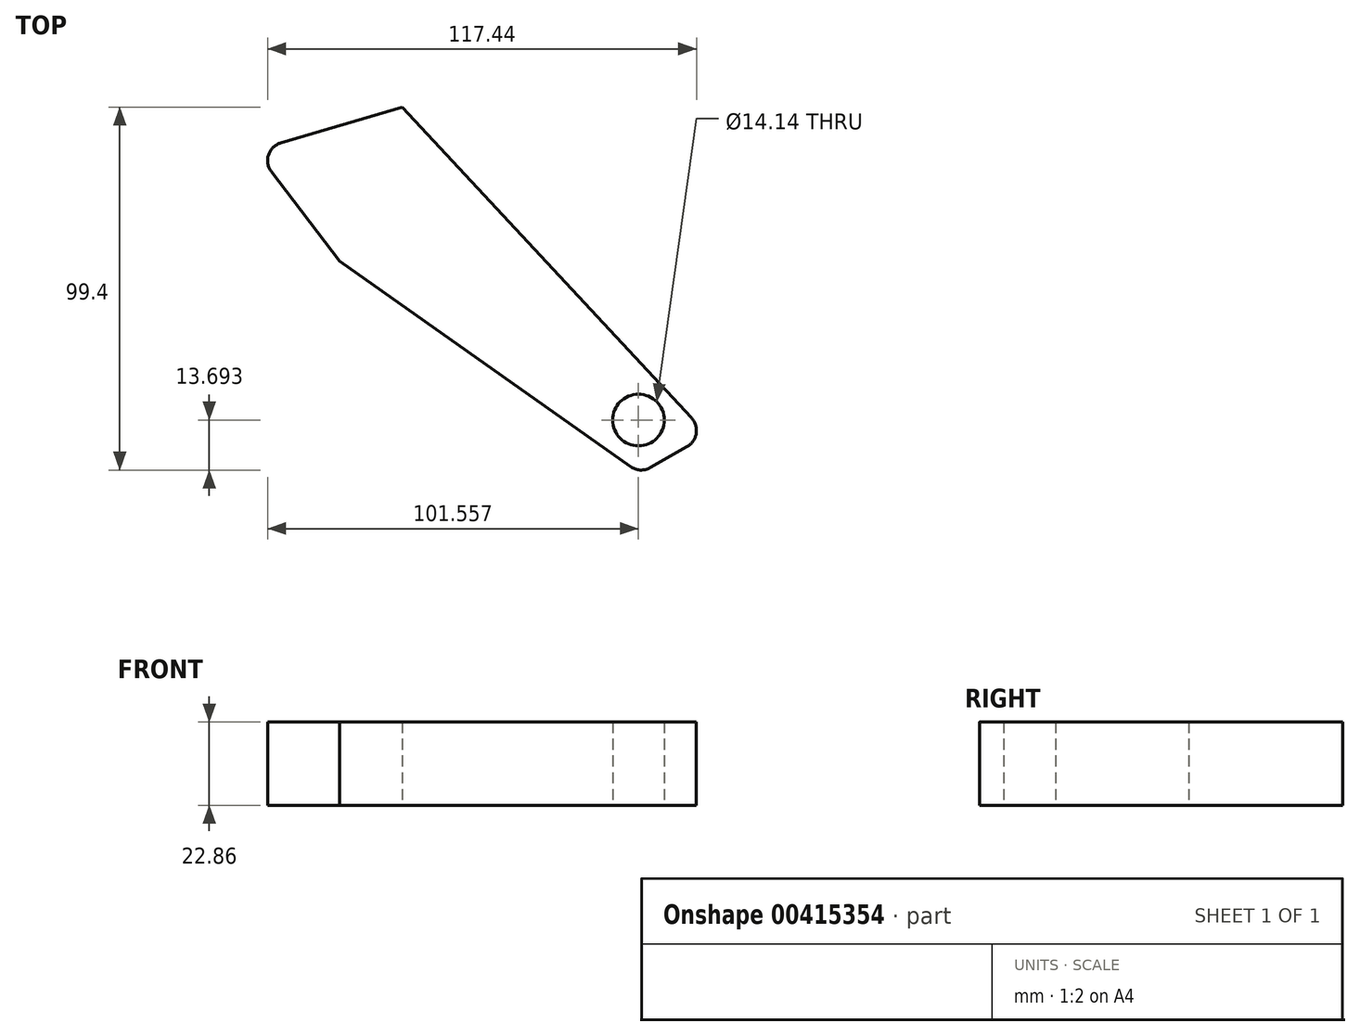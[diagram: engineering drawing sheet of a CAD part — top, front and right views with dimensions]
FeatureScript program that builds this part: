
annotation { "Feature Type Name" : "Feature", "Feature Type Description" : "" }
export const myFeature = defineFeature(function(context is Context, id is Id, definition is map)
    precondition{}
    {
        {
            var Q0;
            Q0=qCreatedBy(makeId("Top.planeOp"),FACE);
            var sketch = newSketch(context, id + "F0", { "sketchPlane" : qUnion([Q0])});
            skLineSegment(sketch, "E0", {"start": v(55.04, -31.63) * mm, "end": v(-28.5, 58.2) * mm});
            skLineSegment(sketch, "E1", {"start": v(-68.84, 46.34) * mm, "end": v(-28.5, 58.2) * mm});
            skLineSegment(sketch, "E2", {"start": v(-68.84, 46.34) * mm, "end": v(-45.74, 16.05) * mm});
            skLineSegment(sketch, "E3", {"start": v(-45.74, 16.05) * mm, "end": v(36.6, -42.14) * mm});
            skLineSegment(sketch, "E4", {"start": v(36.6, -42.14) * mm, "end": v(55.04, -31.63) * mm});
            skSolve(sketch);
        }
        {
            var Q0;
            Q0 = qSketchRegion(id + "F0", true);
            extrude(context, id + "F1", {"entities" : qUnion([Q0]), "depth" : 0.03 * yard});
        }
        {
            var Q0;
            Q0=makeQuery(id+"F1.opExtrude","SWEPT_EDGE",EDGE,{"disambiguationData":[OSD([sQuery(id+"F0.wireOp",EDGE,"E1"),sQuery(id+"F0.wireOp",EDGE,"E2")])]});
            fillet(context, id + "F2", {"entities" : qUnion([Q0]), "radius" : 5.08 * mm, "tangentPropagation" : true, "allowEdgeOverflow" : false});
        }
        {
            var Q0;
            Q0=makeQuery(id+"F1.opExtrude","SWEPT_EDGE",EDGE,{"disambiguationData":[OSD([sQuery(id+"F0.wireOp",EDGE,"E3"),sQuery(id+"F0.wireOp",EDGE,"E4")])]});
            fillet(context, id + "F3", {"entities" : qUnion([Q0]), "radius" : 5.08 * mm, "tangentPropagation" : true, "allowEdgeOverflow" : false});
        }
        {
            var Q0;
            Q0=makeQuery(id+"F1.opExtrude","SWEPT_EDGE",EDGE,{"disambiguationData":[OSD([sQuery(id+"F0.wireOp",EDGE,"E0"),sQuery(id+"F0.wireOp",EDGE,"E4")])]});
            fillet(context, id + "F4", {"entities" : qUnion([Q0]), "radius" : 5.08 * mm, "tangentPropagation" : true, "allowEdgeOverflow" : false});
        }
        {
            var Q0;
            Q0=makeQuery(id+"F1.opExtrude","CAP_FACE",FACE,{"disambiguationData":[OSD([sQuery(id+"F0.wireOp",EDGE,"E0"),sQuery(id+"F0.wireOp",EDGE,"E1"),sQuery(id+"F0.wireOp",EDGE,"E2"),sQuery(id+"F0.wireOp",EDGE,"E3"),sQuery(id+"F0.wireOp",EDGE,"E4")])],"isStart":true});
            var sketch = newSketch(context, id + "F5", { "sketchPlane" : qUnion([Q0])});
            skCircle(sketch, "E5", {"center": v(36.16, 27.52) * mm, "radius": 7.07 * mm});
            skSolve(sketch);
        }
        {
            var Q0;
            Q0=makeQuery(id+"F5.imprint","IMPRINT",FACE,{"disambiguationData":[TD([[makeQuery(id+"F5.imprint","IMPRINT",EDGE,{"derivedFrom":sQuery(id+"F5.wireOp",EDGE,"E5")}),1.0]])]});
            extrude(context, id + "F6", {"entities" : qUnion([Q0]), "operationType" : NewBodyOperationType.REMOVE, "oppositeDirection" : true, "depth" : 75.62 * mm});
        }
    });
